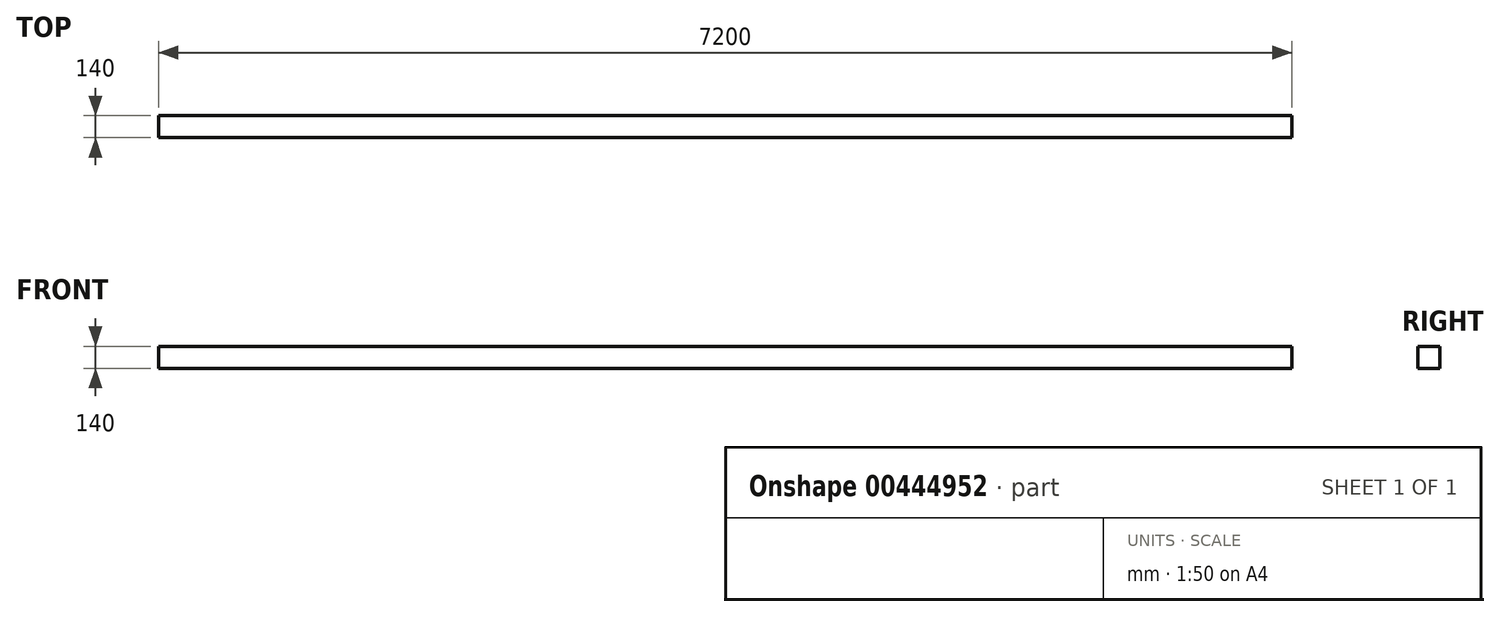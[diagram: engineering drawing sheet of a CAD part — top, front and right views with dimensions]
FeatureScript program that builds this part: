
annotation { "Feature Type Name" : "Feature", "Feature Type Description" : "" }
export const myFeature = defineFeature(function(context is Context, id is Id, definition is map)
    precondition{}
    {
        {
            var Q0;
            Q0=qCreatedBy(makeId("Front.planeOp"),FACE);
            var sketch = newSketch(context, id + "F0", { "sketchPlane" : qUnion([Q0])});
            skLineSegment(sketch, "E0.bottom", {"start": v(3600, -70) * mm, "end": v(-3600, -70) * mm});
            skLineSegment(sketch, "E0.top", {"start": v(3600, 70) * mm, "end": v(-3600, 70) * mm});
            skLineSegment(sketch, "E0.left", {"start": v(3600, -70) * mm, "end": v(3600, 70) * mm});
            skLineSegment(sketch, "E0.right", {"start": v(-3600, -70) * mm, "end": v(-3600, 70) * mm});
            skPoint(sketch, "E0.middle", {"position": v(0, 0) * mm});
            skSolve(sketch);
        }
        {
            var Q0;
            Q0 = qSketchRegion(id + "F0", true);
            extrude(context, id + "F1", {"entities" : qUnion([Q0]), "depth" : 140 * mm});
        }
    });
